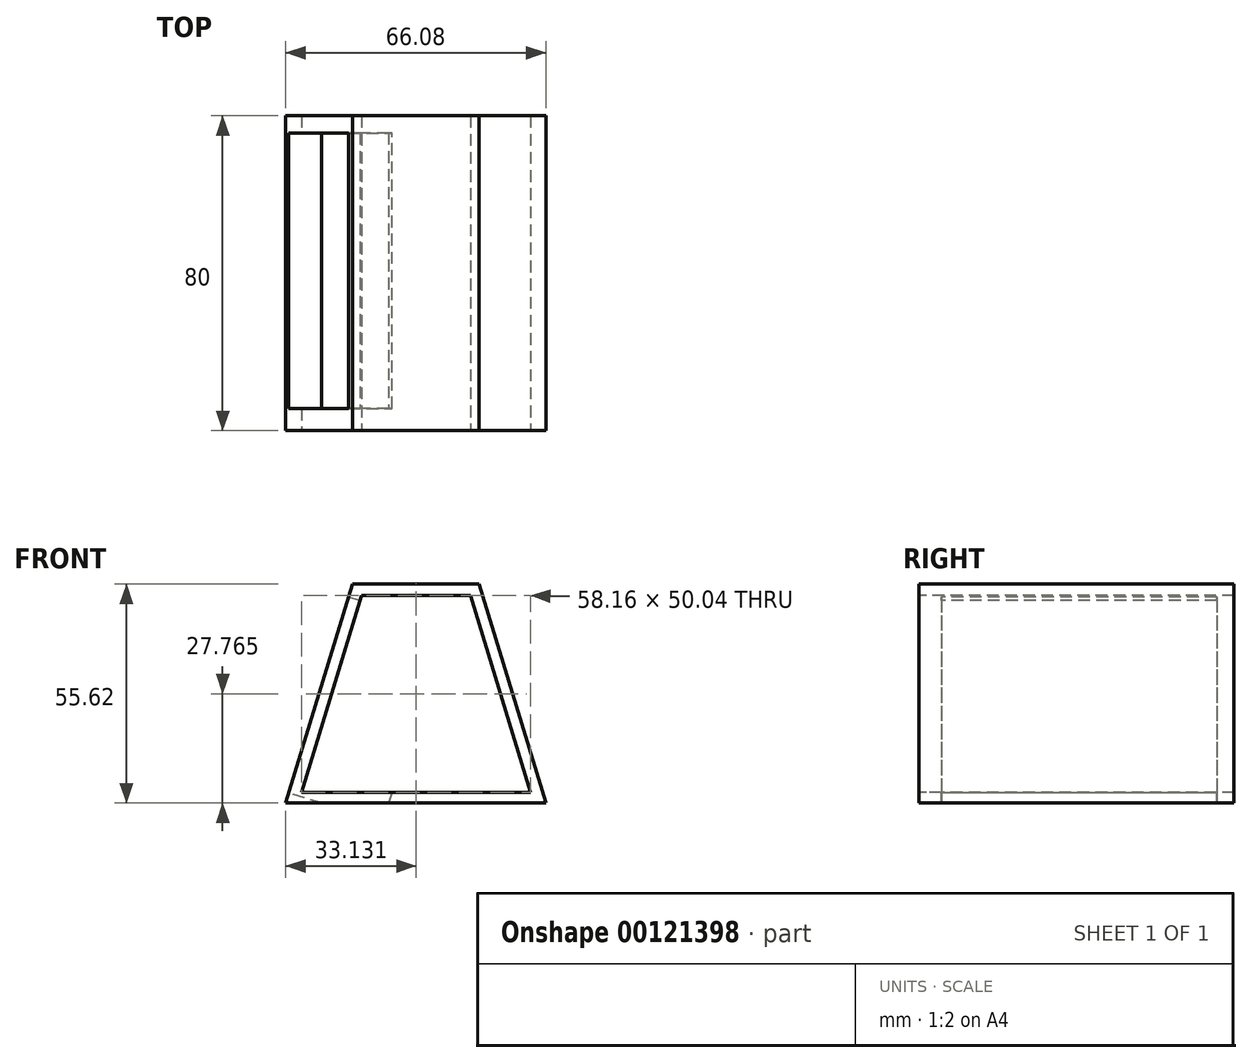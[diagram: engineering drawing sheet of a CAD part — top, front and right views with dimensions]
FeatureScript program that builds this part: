
annotation { "Feature Type Name" : "Feature", "Feature Type Description" : "" }
export const myFeature = defineFeature(function(context is Context, id is Id, definition is map)
    precondition{}
    {
        {
            var Q0;
            Q0=qCreatedBy(makeId("Front.planeOp"),FACE);
            var sketch = newSketch(context, id + "F0", { "sketchPlane" : qUnion([Q0])});
            skLineSegment(sketch, "E0", {"start": v(-33.04, 0) * mm, "end": v(33.04, 0) * mm});
            skLineSegment(sketch, "E1", {"start": v(33.04, 0) * mm, "end": v(16.12, 55.62) * mm});
            skLineSegment(sketch, "E2", {"start": v(16.12, 55.62) * mm, "end": v(-16.12, 55.62) * mm});
            skLineSegment(sketch, "E3", {"start": v(-16.12, 55.62) * mm, "end": v(-33.04, 0) * mm});
            skLineSegment(sketch, "E4", {"start": v(0, 55.62) * mm, "end": v(0, 0) * mm});
            skSolve(sketch);
        }
        {
            var Q0;
            Q0 = qSketchRegion(id + "F0", true);
            var Q1;
            {var subQ0=sQuery(id+"F0.wireOp",EDGE,"E1");Q1=makeQuery(id+"F0.imprint","IMPRINT",FACE,{"disambiguationData":[TD([[makeQuery(id+"F0.imprint","IMPRINT",EDGE,{"derivedFrom":subQ0}),1.0]])]});}
            extrude(context, id + "F1", {"entities" : qUnion([Q0, Q1]), "depth" : 80 * mm});
        }
        {
            var Q0;
            Q0=makeQuery(id+"F1.opExtrude","CAP_FACE",FACE,{"disambiguationData":[OSD([sQuery(id+"F0.wireOp",EDGE,"E0"),sQuery(id+"F0.wireOp",EDGE,"E1"),sQuery(id+"F0.wireOp",EDGE,"E2"),sQuery(id+"F0.wireOp",EDGE,"E3")])],"isStart":false});
            var sketch = newSketch(context, id + "F2", { "sketchPlane" : qUnion([Q0])});
            skLineSegment(sketch, "E5", {"start": v(-29, 2.74) * mm, "end": v(29.17, 2.74) * mm});
            skLineSegment(sketch, "E6", {"start": v(29.17, 2.74) * mm, "end": v(13.95, 52.79) * mm});
            skLineSegment(sketch, "E7", {"start": v(13.95, 52.79) * mm, "end": v(-13.76, 52.79) * mm});
            skLineSegment(sketch, "E8", {"start": v(-13.76, 52.79) * mm, "end": v(-29, 2.74) * mm});
            skSolve(sketch);
        }
        {
            var Q0;
            Q0=makeQuery(id+"F2.imprint","IMPRINT",FACE,{"disambiguationData":[TD([[makeQuery(id+"F2.imprint","IMPRINT",EDGE,{"derivedFrom":sQuery(id+"F2.wireOp",EDGE,"E5")}),1.0]])]});
            extrude(context, id + "F3", {"entities" : qUnion([Q0]), "operationType" : NewBodyOperationType.REMOVE, "oppositeDirection" : true, "depth" : 80 * mm});
        }
        {
            var Q0;
            Q0=makeQuery(id+"F1.opExtrude","SWEPT_FACE",FACE,{"disambiguationData":[OSD([sQuery(id+"F0.wireOp",EDGE,"E3")])]});
            var sketch = newSketch(context, id + "F4", { "sketchPlane" : qUnion([Q0])});
            skLineSegment(sketch, "E9", {"start": v(4.35, 45.08) * mm, "end": v(74.38, 45.08) * mm});
            skLineSegment(sketch, "E10", {"start": v(4.35, 45.08) * mm, "end": v(4.35, -6.96) * mm});
            skLineSegment(sketch, "E11", {"start": v(3.86, -6.96) * mm, "end": v(74.38, -6.96) * mm});
            skLineSegment(sketch, "E12", {"start": v(74.38, 45.08) * mm, "end": v(74.38, -6.96) * mm});
            skSolve(sketch);
        }
        {
            var Q0;
            Q0=makeQuery(id+"F4.imprint","IMPRINT",FACE,{"disambiguationData":[TD([[makeQuery(id+"F4.imprint","IMPRINT",EDGE,{"derivedFrom":sQuery(id+"F4.wireOp",EDGE,"E9")}),-1.0]])]});
            extrude(context, id + "F5", {"entities" : qUnion([Q0]), "operationType" : NewBodyOperationType.REMOVE, "oppositeDirection" : true, "depth" : 25 * mm});
        }
    });
